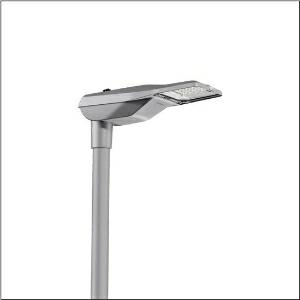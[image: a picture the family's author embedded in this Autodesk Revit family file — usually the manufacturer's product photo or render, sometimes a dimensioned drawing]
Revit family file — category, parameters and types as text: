
# Revit family: streetlight_sl_21_micro___st1_5a_5xe1p33s08db_10f0
name_source: partatom
category: Lighting Fixtures
units: mm (PartAtom-declared; Revit-internal decimal feet)

## family parameters
Cut with Voids When Loaded = No
Host = Face
Light Source = No
Part Type = Normal
Room Calculation Point = No
Round Connector Dimension = Use Diameter
Shared = No

## types (1)
- --- (1 x LED, 5020 lm, 39.1 W, 3000K)
    Apparent Load = 39 VA
    CIE Flux Codes = 22 53 95 100 100
    Color Rendering = 70
    Color Temperature = 3000K
    Default Elevation = 1800 mm
    Description = Streetlight SL 21 micro, mast luminaire, primary light control with lens, of PMMA, primary optical cover: cover, of toughened safety glass, transparent, light distribution: ST1.5a, light emission: direct distribution, primary light characteristic: asymmetric, installation type: side-entry, post-top, LED, High Power LED, rated luminous flux: 5.020lm, luminous efficacy: 128lm/W, light colour: 730, colour temperature: 3000K, control gear: D4i, control: flexible luminous flux parameterisation, time-dependent luminous flux control, constant luminous flux control, overheat protection, pre-setting: logarithmic dimming characteristic, mains connection: 220..240V, AC, 50/60Hz, start of lifetime: 39W, end of service life: 41W, reduction: 18W, luminaire housing, of diecast aluminium, powder-coated, Siteco® metallic grey (DB 702S), corrosivity category C5 mid according to DIN EN ISO 12944, please order mast flange separately, inclination adjustable: 0°, 5°, 10°, 15°, sealing non-destructively replaceable, multi-level sealing system, length: 528mm, width: 235mm, height: 110mm, mast flange for spigot size: 42mm (side-entry): 5XC10008XM4, 60/48mm (side-entry/post-top): 5XC10108XM2, 76/60mm (side-entry/post-top): 5XC10108XM1, Smart Interface above, protection rating (complete): IP66, insulation class (complete): insulation class II (safety insulation), certification: CE, ENEC, ENEC+, VDE, impact resistance: IK10, permissible operating ambient temperature for outdoor applications: -40..+50°C, standard-compliant lighting for roads and squares, packaging unit: 1 piece

Light Distribution: ST1.5a
    Height = 110 mm
    Lamp = 1 x LED
    Lamp Light Flux = 5020 lm
    Lamp Power = 39.1 W
    Lamp count = 1
    Length = 528 mm
    Luminous efficacy = 128 lm/W
    Manufacturer = Siteco
    ModVariant = No
    Model = 5XE1P33S08DB
    Number of Poles = 1
    OnlyDefault = Yes
    Power Factor = 1
    Product Name = Streetlight SL 21 micro | ST1.5a
    Product group = mast luminaire | pylon top
    ProductGroupID = 6100
    Protection Class = Protection class II
    Protection Degree = IP 66
    RLX_Detail_Level = 1
    RLX_Emergency_Light_Flux = 0 lm
    RLX_Emergency_Type = 0
    RLX_Emergency_Type_DB = No
    RlxData = <blob elided: 102561 chars, md5=64833645>
    Socket = socket
    Standby Power = 0 W
    System Light Flux = 5020 lm
    System Power = 39 W
    Type Comments = factory setting: luminous flux: 100 % | dim-lin: 254 | 765 mA
    Type Image = l_1277292.jpg
    URL = http://relux.com
    VarID = @adj_175229
    Voltage = 0 V
    Weight = 0.00 kg
    Width = 235 mm

## geometry (parser evidence)
native form markers: Blend x4, Sweep x10
no freeform markers — native parametric forms only
